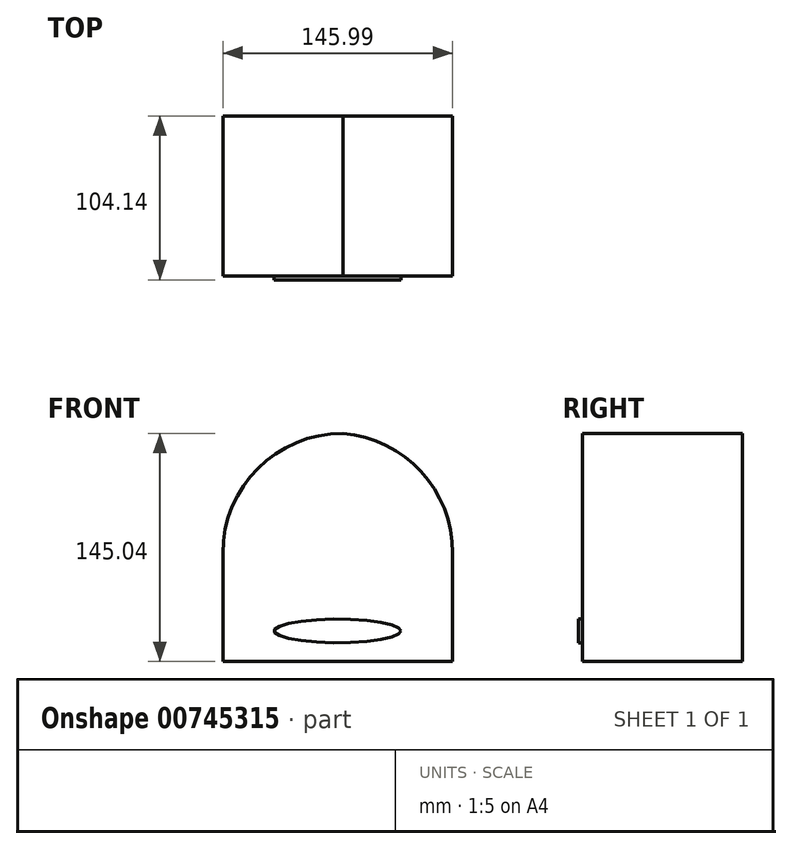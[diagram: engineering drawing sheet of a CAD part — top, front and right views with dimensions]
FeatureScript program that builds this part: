
annotation { "Feature Type Name" : "Feature", "Feature Type Description" : "" }
export const myFeature = defineFeature(function(context is Context, id is Id, definition is map)
    precondition{}
    {
        {
            var Q0;
            Q0=qCreatedBy(makeId("Front.planeOp"),FACE);
            var sketch = newSketch(context, id + "F0", { "sketchPlane" : qUnion([Q0])});
            skLineSegment(sketch, "E0.bottom", {"start": v(-72.9, 73.47) * mm, "end": v(73.09, 73.47) * mm});
            skLineSegment(sketch, "E0.top", {"start": v(-72.9, -71.57) * mm, "end": v(73.09, -71.57) * mm});
            skLineSegment(sketch, "E0.left", {"start": v(-72.9, 73.47) * mm, "end": v(-72.9, -71.57) * mm});
            skLineSegment(sketch, "E0.right", {"start": v(73.09, 73.47) * mm, "end": v(73.09, -71.57) * mm});
            skSolve(sketch);
        }
        {
            var Q0;
            Q0 = qSketchRegion(id + "F0", true);
            extrude(context, id + "F1", {"entities" : qUnion([Q0]), "depth" : 101.6 * mm, "offsetDistance" : 25.4 * mm});
        }
        {
            var Q0;
            Q0=makeQuery(id+"F1.opExtrude","SWEPT_EDGE",EDGE,{"disambiguationData":[OSD([sQuery(id+"F0.wireOp",EDGE,"E0.bottom"),sQuery(id+"F0.wireOp",EDGE,"E0.left")])]});
            fillet(context, id + "F2", {"entities" : qUnion([Q0]), "radius" : 76.2 * mm, "tangentPropagation" : true, "allowEdgeOverflow" : false});
        }
        {
            var Q0;
            Q0=makeQuery(id+"F1.opExtrude","SWEPT_EDGE",EDGE,{"disambiguationData":[OSD([sQuery(id+"F0.wireOp",EDGE,"E0.bottom"),sQuery(id+"F0.wireOp",EDGE,"E0.right")])]});
            fillet(context, id + "F3", {"entities" : qUnion([Q0]), "radius" : 76.2 * mm, "tangentPropagation" : true, "allowEdgeOverflow" : false});
        }
        {
            var Q0;
            Q0=makeQuery(id+"F1.opExtrude","CAP_FACE",FACE,{"disambiguationData":[OSD([sQuery(id+"F0.wireOp",EDGE,"E0.bottom"),sQuery(id+"F0.wireOp",EDGE,"E0.top"),sQuery(id+"F0.wireOp",EDGE,"E0.left"),sQuery(id+"F0.wireOp",EDGE,"E0.right")])],"isStart":false});
            var sketch = newSketch(context, id + "F4", { "sketchPlane" : qUnion([Q0])});
            skEllipse(sketch, "E1", {"center": v(0, -52.04) * mm, "majorRadius": 40.29 * mm, "minorRadius": 7.54 * mm, "majorAxis": v(1, 0)});
            skSolve(sketch);
        }
        {
            var Q0;
            Q0 = qSketchRegion(id + "F4", true);
            extrude(context, id + "F5", {"entities" : qUnion([Q0]), "operationType" : NewBodyOperationType.ADD, "depth" : 2.54 * mm, "offsetDistance" : 25.4 * mm});
        }
    });
